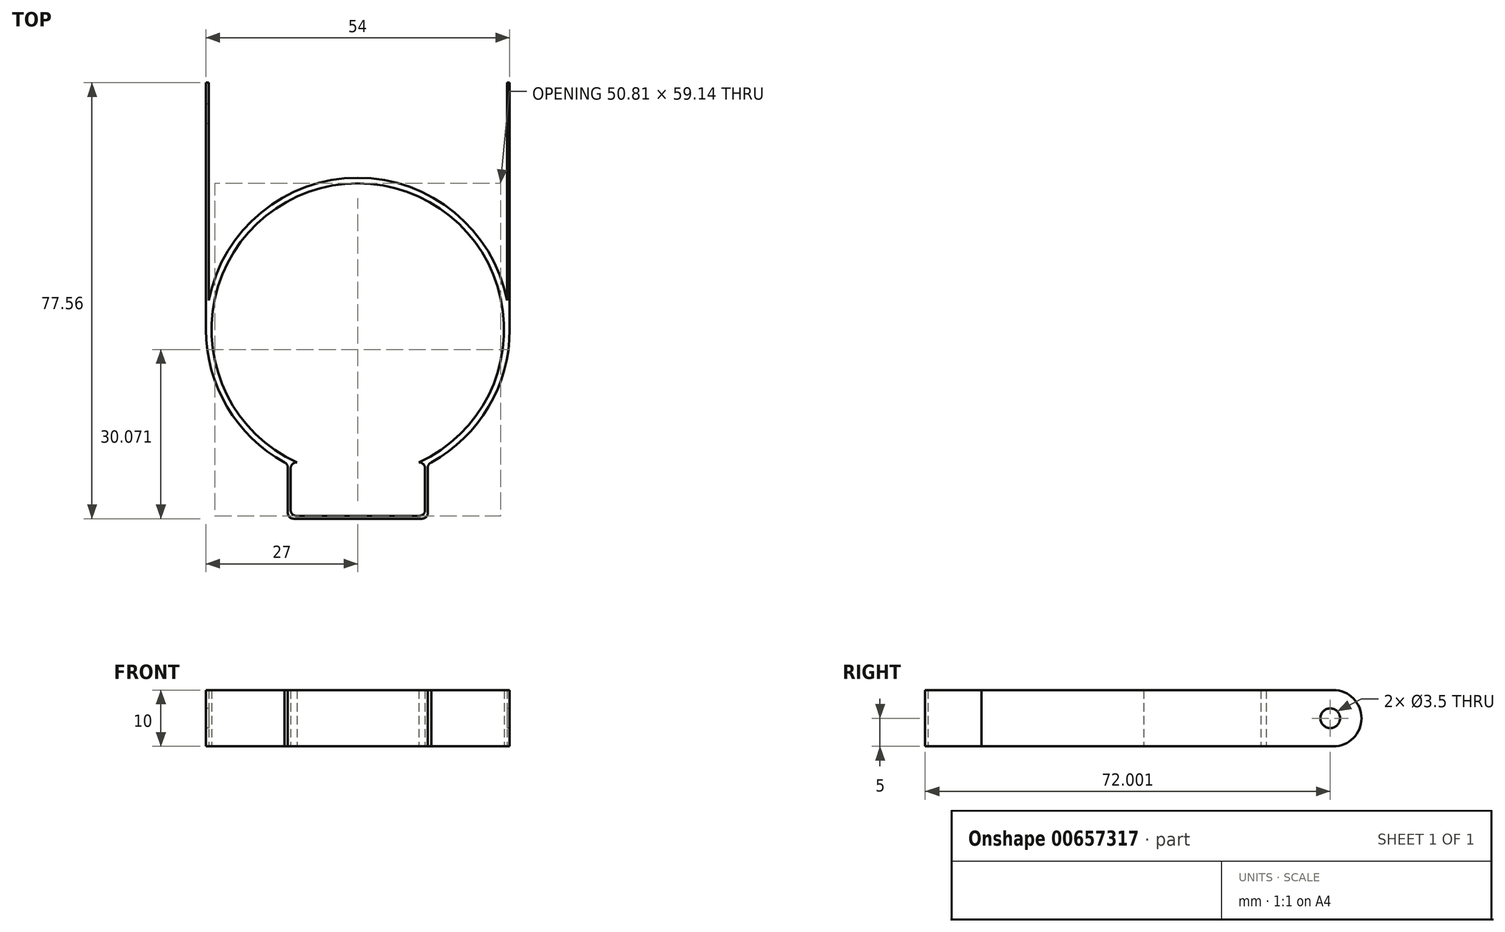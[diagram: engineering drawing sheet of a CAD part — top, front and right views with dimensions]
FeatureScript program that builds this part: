
annotation { "Feature Type Name" : "Feature", "Feature Type Description" : "" }
export const myFeature = defineFeature(function(context is Context, id is Id, definition is map)
    precondition{}
    {
        {
            var Q0;
            Q0=qCreatedBy(makeId("Top.planeOp"),FACE);
            var sketch = newSketch(context, id + "F0", { "sketchPlane" : qUnion([Q0])});
            skArc(sketch, "E0", {"start": v(10.83, -23.64) * mm, "mid": v(0, 26) * mm, "end": v(-10.83, -23.64) * mm});
            skArc(sketch, "E1", {"start": v(13.05, -23.64) * mm, "mid": v(23.25, -13.72) * mm, "end": v(27, 0) * mm});
            skLineSegment(sketch, "E2", {"start": v(-13.05, -23.64) * mm, "end": v(-12.44, -23.64) * mm});
            skLineSegment(sketch, "E3.trimOffspring", {"start": v(10.83, -23.64) * mm, "end": v(11.94, -23.64) * mm});
            skLineSegment(sketch, "E4", {"start": v(-26.5, 5.17) * mm, "end": v(-26.5, 43.92) * mm});
            skLineSegment(sketch, "E5", {"start": v(-26.5, 43.92) * mm, "end": v(-27, 43.92) * mm});
            skLineSegment(sketch, "E6", {"start": v(-27, 43.92) * mm, "end": v(-27, 0) * mm});
            skLineSegment(sketch, "E7", {"start": v(0, 39.75) * mm, "end": v(0, -43.61) * mm, "construction": true});
            skLineSegment(sketch, "E8.MirrorCS", {"start": v(26.5, 43.92) * mm, "end": v(27, 43.92) * mm});
            skLineSegment(sketch, "E9.MirrorCS", {"start": v(26.5, 5.17) * mm, "end": v(26.5, 43.92) * mm});
            skLineSegment(sketch, "E10.MirrorCS", {"start": v(27, 43.92) * mm, "end": v(27, 0) * mm});
            skPoint(sketch, "E11.orphan", {"position": v(-26.5, 0) * mm});
            skPoint(sketch, "E12.MirrorCS.end.orphan", {"position": v(26.5, 0) * mm});
            skArc(sketch, "E13.trimOffspring", {"start": v(26.5, 5.17) * mm, "mid": v(0, 27) * mm, "end": v(-26.5, 5.17) * mm});
            skArc(sketch, "E14.trimOffspring", {"start": v(-27, 0) * mm, "mid": v(-23.25, -13.72) * mm, "end": v(-13.05, -23.64) * mm});
            skLineSegment(sketch, "E15", {"start": v(-11.94, -23.64) * mm, "end": v(-11.94, -33.14) * mm});
            skLineSegment(sketch, "E16", {"start": v(-11.94, -33.14) * mm, "end": v(11.94, -33.14) * mm});
            skPoint(sketch, "E16.endSnap0", {"position": v(11.94, -23.64) * mm});
            skLineSegment(sketch, "E17", {"start": v(11.94, -33.14) * mm, "end": v(11.94, -23.64) * mm});
            skLineSegment(sketch, "E18.0", {"start": v(12.44, -33.64) * mm, "end": v(12.44, -23.64) * mm});
            skLineSegment(sketch, "E18.1", {"start": v(-12.44, -33.64) * mm, "end": v(12.44, -33.64) * mm});
            skLineSegment(sketch, "E18.2", {"start": v(-12.44, -23.64) * mm, "end": v(-12.44, -33.64) * mm});
            skLineSegment(sketch, "E19.trimOffspring", {"start": v(-11.94, -23.64) * mm, "end": v(-10.83, -23.64) * mm});
            skLineSegment(sketch, "E20.trimOffspring", {"start": v(12.44, -23.64) * mm, "end": v(13.05, -23.64) * mm});
            skSolve(sketch);
        }
        {
            var Q0;
            Q0=makeQuery(id+"F0.imprint","IMPRINT",FACE,{"disambiguationData":[TD([[makeQuery(id+"F0.imprint","IMPRINT",EDGE,{"derivedFrom":sQuery(id+"F0.wireOp",EDGE,"E0")}),-1.0]])]});
            extrude(context, id + "F1", {"entities" : qUnion([Q0]), "depth" : 10 * mm, "offsetDistance" : 25 * mm});
        }
        {
            var Q0;
            Q0=makeQuery(id+"F1.opExtrude","SWEPT_FACE",FACE,{"disambiguationData":[OSD([sQuery(id+"F0.wireOp",EDGE,"E6")])]});
            var sketch = newSketch(context, id + "F2", { "sketchPlane" : qUnion([Q0])});
            skCircle(sketch, "E21", {"center": v(-38.36, 5) * mm, "radius": 1.75 * mm});
            skPoint(sketch, "E21.centerSnap0", {"position": v(-43.92, 5) * mm});
            skSolve(sketch);
        }
        {
            var Q0;
            Q0 = qSketchRegion(id + "F2", true);
            extrude(context, id + "F3", {"entities" : qUnion([Q0]), "operationType" : NewBodyOperationType.REMOVE, "oppositeDirection" : true, "depth" : 100 * mm, "offsetDistance" : 25 * mm});
        }
        {
            var Q0;
            Q0=makeQuery(id+"F1.opExtrude","CAP_EDGE",EDGE,{"disambiguationData":[OSD([sQuery(id+"F0.wireOp",EDGE,"E5")])],"isStart":true});
            var Q1;
            Q1=makeQuery(id+"F1.opExtrude","CAP_EDGE",EDGE,{"disambiguationData":[OSD([sQuery(id+"F0.wireOp",EDGE,"E5")])],"isStart":false});
            var Q2;
            Q2=makeQuery(id+"F1.opExtrude","CAP_EDGE",EDGE,{"disambiguationData":[OSD([sQuery(id+"F0.wireOp",EDGE,"E8.MirrorCS")])],"isStart":true});
            var Q3;
            Q3=makeQuery(id+"F1.opExtrude","CAP_EDGE",EDGE,{"disambiguationData":[OSD([sQuery(id+"F0.wireOp",EDGE,"E8.MirrorCS")])],"isStart":false});
            fillet(context, id + "F4", {"entities" : qUnion([Q0, Q1, Q2, Q3]), "radius" : 5 * mm, "tangentPropagation" : true, "allowEdgeOverflow" : false});
        }
        {
            var Q0;
            Q0=makeQuery(id+"F1.opExtrude","SWEPT_EDGE",EDGE,{"disambiguationData":[OSD([sQuery(id+"F0.wireOp",EDGE,"E2"),sQuery(id+"F0.wireOp",EDGE,"E18.2")])]});
            var Q1;
            Q1=makeQuery(id+"F1.opExtrude","SWEPT_EDGE",EDGE,{"disambiguationData":[OSD([sQuery(id+"F0.wireOp",EDGE,"E15"),sQuery(id+"F0.wireOp",EDGE,"E19.trimOffspring")])]});
            var Q2;
            Q2=makeQuery(id+"F1.opExtrude","SWEPT_EDGE",EDGE,{"disambiguationData":[OSD([sQuery(id+"F0.wireOp",EDGE,"E3.trimOffspring"),sQuery(id+"F0.wireOp",EDGE,"E17")])]});
            var Q3;
            Q3=makeQuery(id+"F1.opExtrude","SWEPT_EDGE",EDGE,{"disambiguationData":[OSD([sQuery(id+"F0.wireOp",EDGE,"E18.0"),sQuery(id+"F0.wireOp",EDGE,"E20.trimOffspring")])]});
            var Q4;
            Q4=makeQuery(id+"F1.opExtrude","SWEPT_EDGE",EDGE,{"disambiguationData":[OSD([sQuery(id+"F0.wireOp",EDGE,"E15"),sQuery(id+"F0.wireOp",EDGE,"E16")])]});
            var Q5;
            Q5=makeQuery(id+"F1.opExtrude","SWEPT_EDGE",EDGE,{"disambiguationData":[OSD([sQuery(id+"F0.wireOp",EDGE,"E16"),sQuery(id+"F0.wireOp",EDGE,"E17")])]});
            var Q6;
            Q6=makeQuery(id+"F1.opExtrude","SWEPT_EDGE",EDGE,{"disambiguationData":[OSD([sQuery(id+"F0.wireOp",EDGE,"E18.1"),sQuery(id+"F0.wireOp",EDGE,"E18.2")])]});
            var Q7;
            Q7=makeQuery(id+"F1.opExtrude","SWEPT_EDGE",EDGE,{"disambiguationData":[OSD([sQuery(id+"F0.wireOp",EDGE,"E18.0"),sQuery(id+"F0.wireOp",EDGE,"E18.1")])]});
            fillet(context, id + "F5", {"entities" : qUnion([Q0, Q1, Q2, Q3, Q4, Q5, Q6, Q7]), "radius" : 1 * mm, "tangentPropagation" : true, "allowEdgeOverflow" : false});
        }
    });
